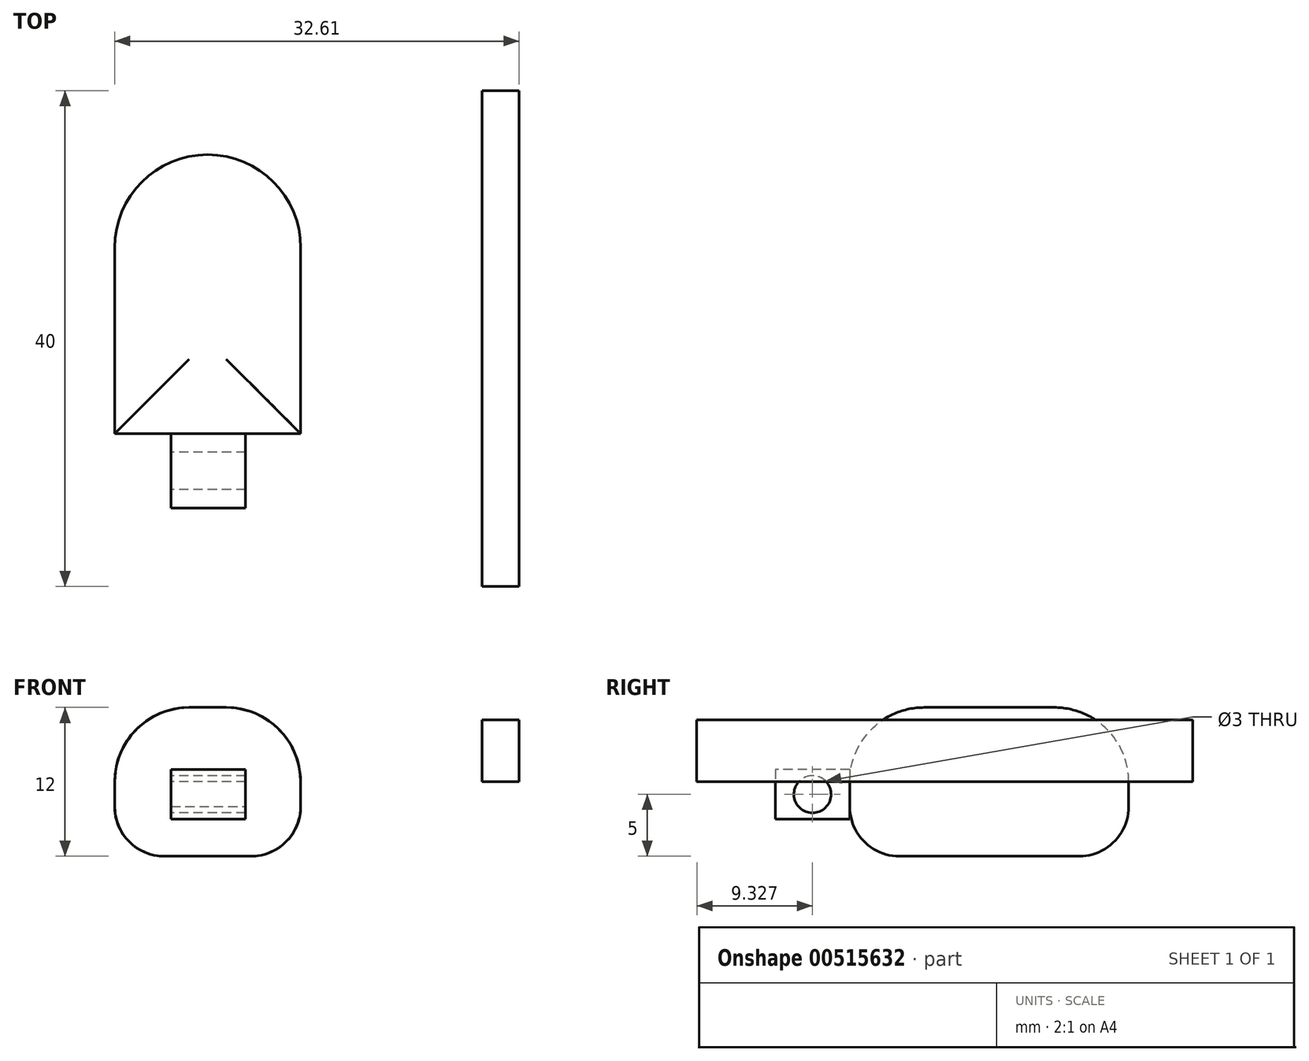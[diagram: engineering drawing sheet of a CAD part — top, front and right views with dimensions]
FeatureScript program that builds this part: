
annotation { "Feature Type Name" : "Feature", "Feature Type Description" : "" }
export const myFeature = defineFeature(function(context is Context, id is Id, definition is map)
    precondition{}
    {
        {
            var Q0;
            Q0=qCreatedBy(makeId("Top.planeOp"),FACE);
            var sketch = newSketch(context, id + "F0", { "sketchPlane" : qUnion([Q0])});
            skCircle(sketch, "E0", {"center": v(-58.19, 52.45) * mm, "radius": 7.5 * mm});
            skLineSegment(sketch, "E1.bottom", {"start": v(-65.69, 52.45) * mm, "end": v(-50.69, 52.45) * mm, "construction": true});
            skLineSegment(sketch, "E1.top", {"start": v(-65.69, 37.45) * mm, "end": v(-50.69, 37.45) * mm});
            skLineSegment(sketch, "E1.left", {"start": v(-65.69, 52.45) * mm, "end": v(-65.69, 37.45) * mm});
            skLineSegment(sketch, "E1.right", {"start": v(-50.69, 52.45) * mm, "end": v(-50.69, 37.45) * mm});
            skLineSegment(sketch, "E2.bottom", {"start": v(-61.19, 37.45) * mm, "end": v(-55.19, 37.45) * mm});
            skLineSegment(sketch, "E3", {"start": v(-58.19, 59.95) * mm, "end": v(-58.19, 37.45) * mm, "construction": true});
            skSolve(sketch);
        }
        {
            var Q0;
            Q0 = qSketchRegion(id + "F0", true);
            extrude(context, id + "F1", {"entities" : qUnion([Q0]), "endBound" : BoundingType.SYMMETRIC, "depth" : 12 * mm, "offsetDistance" : 25 * mm});
        }
        {
            var Q0;
            Q0=makeQuery(id+"F1.opExtrude","CAP_FACE",FACE,{"disambiguationData":[OSD([sQuery(id+"F0.wireOp",EDGE,"E0"),sQuery(id+"F0.wireOp",EDGE,"E1.top"),sQuery(id+"F0.wireOp",EDGE,"E1.left"),sQuery(id+"F0.wireOp",EDGE,"E1.right"),sQuery(id+"F0.wireOp",EDGE,"E2.top"),sQuery(id+"F0.wireOp",EDGE,"E2.left"),sQuery(id+"F0.wireOp",EDGE,"E2.right")])],"isStart":false});
            fillet(context, id + "F2", {"entities" : qUnion([Q0]), "radius" : 6 * mm, "tangentPropagation" : true, "allowEdgeOverflow" : false});
        }
        {
            var Q0;
            Q0=makeQuery(id+"F1.opExtrude","CAP_FACE",FACE,{"disambiguationData":[OSD([sQuery(id+"F0.wireOp",EDGE,"E0"),sQuery(id+"F0.wireOp",EDGE,"E1.top"),sQuery(id+"F0.wireOp",EDGE,"E1.left"),sQuery(id+"F0.wireOp",EDGE,"E1.right"),sQuery(id+"F0.wireOp",EDGE,"E2.bottom")])],"isStart":true});
            fillet(context, id + "F3", {"entities" : qUnion([Q0]), "radius" : 4 * mm, "tangentPropagation" : true, "allowEdgeOverflow" : false});
        }
        {
            var Q0;
            Q0=qCreatedBy(makeId("Top.planeOp"),FACE);
            var sketch = newSketch(context, id + "F4", { "sketchPlane" : qUnion([Q0])});
            skLineSegment(sketch, "E4.bottom", {"start": v(-55.14, 37.45) * mm, "end": v(-61.14, 37.45) * mm});
            skLineSegment(sketch, "E4.top", {"start": v(-55.14, 31.45) * mm, "end": v(-61.14, 31.45) * mm});
            skLineSegment(sketch, "E4.left", {"start": v(-55.14, 37.45) * mm, "end": v(-55.14, 31.45) * mm});
            skLineSegment(sketch, "E4.right", {"start": v(-61.14, 37.45) * mm, "end": v(-61.14, 31.45) * mm});
            skLineSegment(sketch, "E5", {"start": v(-55.14, 34.45) * mm, "end": v(-61.14, 34.45) * mm, "construction": true});
            skLineSegment(sketch, "E6", {"start": v(-58.14, 37.45) * mm, "end": v(-58.14, 31.45) * mm, "construction": true});
            skSolve(sketch);
        }
        {
            var Q0;
            Q0 = qSketchRegion(id + "F4", true);
            extrude(context, id + "F5", {"entities" : qUnion([Q0]), "operationType" : NewBodyOperationType.ADD, "depth" : 1 * mm, "offsetDistance" : 25 * mm, "hasSecondDirection" : true, "secondDirectionOppositeDirection" : true, "secondDirectionDepth" : 3 * mm});
        }
        {
            var Q0;
            Q0=makeQuery(id+"F5.opExtrude","SWEPT_FACE",FACE,{"disambiguationData":[OSD([sQuery(id+"F4.wireOp",EDGE,"E4.right")])]});
            var sketch = newSketch(context, id + "F6", { "sketchPlane" : qUnion([Q0])});
            skCircle(sketch, "E7", {"center": v(-34.45, -1) * mm, "radius": 1.5 * mm});
            skLineSegment(sketch, "E8", {"start": v(-31.45, -1) * mm, "end": v(-37.45, -1) * mm, "construction": true});
            skLineSegment(sketch, "E9", {"start": v(-34.45, -2.5) * mm, "end": v(-34.45, 0.5) * mm, "construction": true});
            skSolve(sketch);
        }
        {
            var Q0;
            Q0 = qSketchRegion(id + "F6", true);
            extrude(context, id + "F7", {"entities" : qUnion([Q0]), "operationType" : NewBodyOperationType.REMOVE, "oppositeDirection" : true, "depth" : 6 * mm, "offsetDistance" : 25 * mm});
        }
        {
            var Q0;
            Q0=qCreatedBy(makeId("Top.planeOp"),FACE);
            var sketch = newSketch(context, id + "F8", { "sketchPlane" : qUnion([Q0])});
            skLineSegment(sketch, "E10.bottom", {"start": v(-36.08, 65.12) * mm, "end": v(-33.08, 65.12) * mm});
            skLineSegment(sketch, "E10.top", {"start": v(-36.08, 25.12) * mm, "end": v(-33.08, 25.12) * mm});
            skLineSegment(sketch, "E10.left", {"start": v(-36.08, 65.12) * mm, "end": v(-36.08, 25.12) * mm});
            skLineSegment(sketch, "E10.right", {"start": v(-33.08, 65.12) * mm, "end": v(-33.08, 25.12) * mm});
            skSolve(sketch);
        }
        {
            var Q0;
            Q0 = qSketchRegion(id + "F8", true);
            extrude(context, id + "F9", {"entities" : qUnion([Q0]), "depth" : 5 * mm, "offsetDistance" : 25 * mm});
        }
    });
